# Revit family: TY4651
name_source: partatom
category: Sprinklers
revit_build: Autodesk Revit 2016 (Build: 20150220_1215(x64)
units: mm (PartAtom-declared; Revit-internal decimal feet)

## family parameters
Always vertical = Yes
Cut with Voids When Loaded = No
Maintain Annotation Orientation = No
OmniClass Number = 23.65.70.17.11.24
OmniClass Title = Fire Fighting Sprinkler Heads
Part Type = Normal
Room Calculation Point = No
Round Connector Dimension = Use Diameter
Shared = No
Work Plane-Based = No

## types (40) — shared parameters
COBie = Yes
COBie.Component.Name = Sprinklers:Conventional_SIN
COBie.Type = Yes
COBie.Type.AssetType = Fixed
COBie.Type.Category = Pr_70_55_97_84:Sprinklers
COBie.Type.DurationUnit = year
COBie.Type.Manufacturer = Tyco Fire Protection Products
COBie.Type.Material = Bronze
COBie.Type.NominalHeight = 0' - 0"
COBie.Type.NominalLength = 0' - 0"
COBie.Type.NominalWidth = 0' - 0"
Coverage = Standard
K-Factor = 7.9771
Manufacturer = Tyco Fire Protection Products
Manufacturer URL = www.tyco-fire.com
Model = TY-B
Nominal Diameter 1 = 1"
Orifice = Extra Large
Orifice Size = 1"
Outside Diameter 1 = 1"
Response = Standard
SIN No = TY4651
Takeout 1 = 2"
Technical Data Sheet No = TFP661
zero-valued in all types: COBie.Type.ReplacementCost, Style Id

## per-type parameters (varying)
| type | COBie.Component.Description | COBie.Component.InstallationDate | COBie.Component.WarrantyStartDate | COBie.Type.Colour | COBie.Type.Finish | COBie.Type.ModelNumber | COBie.Type.ModelReference | COBie.Type.Shape | COBie.Type.Size | COBie.Type.WarrantyDescription | COBie.Type.WarrantyDurationLabor | COBie.Type.WarrantyDurationParts | COBie.Type.WarrantyDurationUnit | COBie.Type.WarrantyGuarantorParts | Description | Part No | Temperature Rating |
| TY-B Conventional (Old Style) Brass 135°F/57°C 8K ¾" NPT_57-593-1-135 | TY-B Wet Conventional  57.2°C K115 DN20 NPT Br |  |  | Yellow | Natural Brass | 57-593-1-135 | TY-B Wet Conventional  57.2°C K115 DN20 NPT Br | Cylinder | 3/4"(DN20) |  |  |  |  | http://tycofsbp.com | TY-B Conventional (Old Style) Brass 135°F/57°C 8K ¾" NPT_57-593-1-135 | 57-593-1-135 | 135 °F |
| TY-B Conventional (Old Style) Brass 155°F/68°C 8K ¾" NPT_57-593-1-155 | TY-B Wet Conventional  68.3°C K115 DN20 NPT Br |  |  | Yellow | Natural Brass | 57-593-1-155 | TY-B Wet Conventional  68.3°C K115 DN20 NPT Br | Cylinder | 3/4"(DN20) |  |  |  |  | http://tycofsbp.com | TY-B Conventional (Old Style) Brass 155°F/68°C 8K ¾" NPT_57-593-1-155 | 57-593-1-155 | 155 °F |
| TY-B Conventional (Old Style) Brass 175°F/79°C 8K ¾" NPT_57-593-1-175 | TY-B Wet Conventional  79.4°C K115 DN20 NPT Br |  |  | Yellow | Natural Brass | 57-593-1-175 | TY-B Wet Conventional  79.4°C K115 DN20 NPT Br | Cylinder | 3/4"(DN20) |  |  |  |  | http://tycofsbp.com | TY-B Conventional (Old Style) Brass 175°F/79°C 8K ¾" NPT_57-593-1-175 | 57-593-1-175 | 175 °F |
| TY-B Conventional (Old Style) Brass 200°F/93°C 8K ¾" NPT_57-593-1-200 | TY-B Wet Conventional  93.3°C K115 DN20 NPT Br |  |  | Yellow | Natural Brass | 57-593-1-200 | TY-B Wet Conventional  93.3°C K115 DN20 NPT Br | Cylinder | 3/4"(DN20) |  |  |  |  | http://tycofsbp.com | TY-B Conventional (Old Style) Brass 200°F/93°C 8K ¾" NPT_57-593-1-200 | 57-593-1-200 | 200 °F |
| TY-B Conventional (Old Style) Brass 286°F/141°C 8K ¾" NPT_57-593-1-286 | TY-B Wet Conventional  141.1°C K115 DN20 NPT Br |  |  | Yellow | Natural Brass | 57-593-1-286 | TY-B Wet Conventional  141.1°C K115 DN20 NPT Br | Cylinder | 3/4"(DN20) |  |  |  |  | http://tycofsbp.com | TY-B Conventional (Old Style) Brass 286°F/141°C 8K ¾" NPT_57-593-1-286 | 57-593-1-286 | 286 °F |
| TY-B Conventional (Old Style) Brass 360°F/182°C 8K ¾" NPT_57-593-1-360 | TY-B Wet Conventional  182.2°C K115 DN20 NPT Br | 1900-12-31T23:59:59 | 1900-12-31T23:59:59 |  |  | 57-593-1-360 | TY-B Wet Conventional  182.2°C K115 DN20 NPT Br |  | DN20 | On-site Sprinkler Replacement Warranty | 10 | 10 | year |  | TY-B Conventional (Old Style) Brass 360°F/182°C 8K ¾" NPT_57-593-1-360 | 57-593-1-360 | 360 °F |
| TY-B Conventional (Old Style) White 135°F/57°C 8K ¾" NPT_57-593-3-135 | TY-B Wet Conventional  57.2°C K115 DN20 NPT Wh9010 |  |  | White | Pure White | 57-593-3-135 | TY-B Wet Conventional  57.2°C K115 DN20 NPT Wh9010 | Cylinder | 3/4"(DN20) |  |  |  |  | http://tycofsbp.com | TY-B Conventional (Old Style) Brass 135°F/57°C 8K ¾" NPT_57-593-3-135 | 57-593-3-135 | 135 °F |
| TY-B Conventional (Old Style) White 155°F/68°C 8K ¾" NPT_57-593-3-155 | TY-B Wet Conventional  68.3°C K115 DN20 NPT Wh9010 | 1900-12-31T23:59:59 | 1900-12-31T23:59:59 |  |  | 57-593-3-155 | TY-B Wet Conventional  68.3°C K115 DN20 NPT Wh9010 |  | DN20 | On-site Sprinkler Replacement Warranty | 10 | 10 | year |  | TY-B Conventional (Old Style) Brass 155°F/68°C 8K ¾" NPT_57-593-3-155 | 57-593-3-155 | 155 °F |
| TY-B Conventional (Old Style) White 175°F/79°C 8K ¾" NPT_57-593-3-175 | TY-B Wet Conventional  79.4°C K115 DN20 NPT Wh9010 |  |  | White | Pure White | 57-593-3-175 | TY-B Wet Conventional  79.4°C K115 DN20 NPT Wh9010 | Cylinder | 3/4"(DN20) |  |  |  |  | http://tycofsbp.com | TY-B Conventional (Old Style) Brass 175°F/79°C 8K ¾" NPT_57-593-3-175 | 57-593-3-175 | 175 °F |
| TY-B Conventional (Old Style) White 200°F/93°C 8K ¾" NPT_57-593-3-200 | TY-B Wet Conventional  93.3°C K115 DN20 NPT Wh9010 |  |  | White | Pure White | 57-593-3-200 | TY-B Wet Conventional  93.3°C K115 DN20 NPT Wh9010 | Cylinder | 3/4"(DN20) |  |  |  |  | http://tycofsbp.com | TY-B Conventional (Old Style) Brass 200°F/93°C 8K ¾" NPT_57-593-3-200 | 57-593-3-200 | 200 °F |
| TY-B Conventional (Old Style) White 286°F/141°C 8K ¾" NPT_57-593-3-286 | TY-B Wet Conventional  141.1°C K115 DN20 NPT Wh9010 |  |  | White | Pure White | 57-593-3-286 | TY-B Wet Conventional  141.1°C K115 DN20 NPT Wh9010 | Cylinder | 3/4"(DN20) |  |  |  |  | http://tycofsbp.com | TY-B Conventional (Old Style) Brass 286°F/141°C 8K ¾" NPT_57-593-3-286 | 57-593-3-286 | 286 °F |
| TY-B Conventional (Old Style) White 360°F/182°C 8K ¾" NPT_57-593-3-360 | TY-B Wet Conventional  182.2°C K115 DN20 NPT Wh9010 |  |  | White | Pure White | 57-593-3-360 | TY-B Wet Conventional  182.2°C K115 DN20 NPT Wh9010 | Cylinder | 3/4"(DN20) |  |  |  |  | http://tycofsbp.com | TY-B Conventional (Old Style) Brass 360°F/182°C 8K ¾" NPT_57-593-3-360 | 57-593-3-360 | 360 °F |
| TY-B Conventional (Old Style) White 135°F/57°C 8K ¾" NPT_57-593-4-135 | TY-B Wet Conventional  57.2°C K115 DN20 NPT Wh9003 |  |  | White | Signal White | 57-593-4-135 | TY-B Wet Conventional  57.2°C K115 DN20 NPT Wh9003 | Cylinder | 3/4"(DN20) |  |  |  |  | http://tycofsbp.com | TY-B Conventional (Old Style) White 135°F/57°C 8K ¾" NPT_57-593-4-135 | 57-593-4-135 | 135 °F |
| TY-B Conventional (Old Style) White 155°F/68°C 8K ¾" NPT_57-593-4-155 | TY-B Wet Conventional  68.3°C K115 DN20 NPT Wh9003 |  |  | White | Signal White | 57-593-4-155 | TY-B Wet Conventional  68.3°C K115 DN20 NPT Wh9003 | Cylinder | 3/4"(DN20) |  |  |  |  | http://tycofsbp.com | TY-B Conventional (Old Style) White 155°F/68°C 8K ¾" NPT_57-593-4-155 | 57-593-4-155 | 155 °F |
| TY-B Conventional (Old Style) White 175°F/79°C 8K ¾" NPT_57-593-4-175 | TY-B Wet Conventional  79.4°C K115 DN20 NPT Wh9003 |  |  | White | Signal White | 57-593-4-175 | TY-B Wet Conventional  79.4°C K115 DN20 NPT Wh9003 | Cylinder | 3/4"(DN20) |  |  |  |  | http://tycofsbp.com | TY-B Conventional (Old Style) White 175°F/79°C 8K ¾" NPT_57-593-4-175 | 57-593-4-175 | 175 °F |
| TY-B Conventional (Old Style) White 200°F/93°C 8K ¾" NPT_57-593-4-200 | TY-B Wet Conventional  93.3°C K115 DN20 NPT Wh9003 |  |  | White | Signal White | 57-593-4-200 | TY-B Wet Conventional  93.3°C K115 DN20 NPT Wh9003 | Cylinder | 3/4"(DN20) |  |  |  |  | http://tycofsbp.com | TY-B Conventional (Old Style) White 200°F/93°C 8K ¾" NPT_57-593-4-200 | 57-593-4-200 | 200 °F |
| TY-B Conventional (Old Style) White 286°F/141°C 8K ¾" NPT_57-593-4-286 | TY-B Wet Conventional  141.1°C K115 DN20 NPT Wh9003 |  |  | White | Signal White | 57-593-4-286 | TY-B Wet Conventional  141.1°C K115 DN20 NPT Wh9003 | Cylinder | 3/4"(DN20) |  |  |  |  | http://tycofsbp.com | TY-B Conventional (Old Style) White 286°F/141°C 8K ¾" NPT_57-593-4-286 | 57-593-4-286 | 286 °F |
| TY-B Conventional (Old Style) White 360°F/182°C 8K ¾" NPT_57-593-4-360 | TY-B Wet Conventional  182.2°C K115 DN20 NPT Wh9003 |  |  | White | Signal White | 57-593-4-360 | TY-B Wet Conventional  182.2°C K115 DN20 NPT Wh9003 | Cylinder | 3/4"(DN20) |  |  |  |  | http://tycofsbp.com | TY-B Conventional (Old Style) White 360°F/182°C 8K ¾" NPT_57-593-4-360 | 57-593-4-360 | 360 °F |
| TY-B Conventional (Old Style) Wax 135°F/57°C 8K ¾" NPT_57-593-6-135 | TY-B Wet Conventional  57.2°C K115 DN20 NPT Wx |  |  | Gray | Wax Coated | 57-593-6-135 | TY-B Wet Conventional  57.2°C K115 DN20 NPT Wx | Cylinder | 3/4"(DN20) |  |  |  |  | http://tycofsbp.com | TY-B Conventional (Old Style) Wax 135°F/57°C 8K ¾" NPT_57-593-6-135 | 57-593-6-135 | 135 °F |
| TY-B Conventional (Old Style) Wax 155°F/68°C 8K ¾" NPT_57-593-6-155 | TY-B Wet Conventional  68.3°C K115 DN20 NPT Wx |  |  | Gray | Wax Coated | 57-593-6-155 | TY-B Wet Conventional  68.3°C K115 DN20 NPT Wx | Cylinder | 3/4"(DN20) |  |  |  |  | http://tycofsbp.com | TY-B Conventional (Old Style) Wax 155°F/68°C 8K ¾" NPT_57-593-6-155 | 57-593-6-155 | 155 °F |
| TY-B Conventional (Old Style) Wax 175°F/79°C 8K ¾" NPT_57-593-6-175 | TY-B Wet Conventional  79.4°C K115 DN20 NPT Wx |  |  | Gray | Wax Coated | 57-593-6-175 | TY-B Wet Conventional  79.4°C K115 DN20 NPT Wx | Cylinder | 3/4"(DN20) |  |  |  |  | http://tycofsbp.com | TY-B Conventional (Old Style) Wax 175°F/79°C 8K ¾" NPT_57-593-6-175 | 57-593-6-175 | 175 °F |
| TY-B Conventional (Old Style) Wax 200°F/93°C 8K ¾" NPT_57-593-6-200 | TY-B Wet Conventional  93.3°C K115 DN20 NPT Wx |  |  | Gray | Wax Coated | 57-593-6-200 | TY-B Wet Conventional  93.3°C K115 DN20 NPT Wx | Cylinder | 3/4"(DN20) |  |  |  |  | http://tycofsbp.com | TY-B Conventional (Old Style) Wax 200°F/93°C 8K ¾" NPT_57-593-6-200 | 57-593-6-200 | 200 °F |
| TY-B Conventional (Old Style) Wax 286°F/141°C 8K ¾" NPT_57-593-6-286 | TY-B Wet Conventional  141.1°C K115 DN20 NPT Wx |  |  | Gray | Wax Coated | 57-593-6-286 | TY-B Wet Conventional  141.1°C K115 DN20 NPT Wx | Cylinder | 3/4"(DN20) |  |  |  |  | http://tycofsbp.com | TY-B Conventional (Old Style) Wax 286°F/141°C 8K ¾" NPT_57-593-6-286 | 57-593-6-286 | 286 °F |
| TY-B Conventional (Old Style) Lead 135°F/57°C 8K ¾" NPT_57-593-7-135 | TY-B Wet Conventional  57.2°C K115 DN20 NPT Lead |  |  | Gray | Lead Coated | 57-593-7-135 | TY-B Wet Conventional  57.2°C K115 DN20 NPT Lead | Cylinder | 3/4"(DN20) |  |  |  |  | http://tycofsbp.com | TY-B Conventional (Old Style) Lead 135°F/57°C 8K ¾" NPT_57-593-7-135 | 57-593-7-135 | 135 °F |
| TY-B Conventional (Old Style) Lead 155°F/68°C 8K ¾" NPT_57-593-7-155 | TY-B Wet Conventional  68.3°C K115 DN20 NPT Lead |  |  | Gray | Lead Coated | 57-593-7-155 | TY-B Wet Conventional  68.3°C K115 DN20 NPT Lead | Cylinder | 3/4"(DN20) |  |  |  |  | http://tycofsbp.com | TY-B Conventional (Old Style) Lead 155°F/68°C 8K ¾" NPT_57-593-7-155 | 57-593-7-155 | 155 °F |
| TY-B Conventional (Old Style) Lead 175°F/79°C 8K ¾" NPT_57-593-7-175 | TY-B Wet Conventional  79.4°C K115 DN20 NPT Lead |  |  | Gray | Lead Coated | 57-593-7-175 | TY-B Wet Conventional  79.4°C K115 DN20 NPT Lead | Cylinder | 3/4"(DN20) |  |  |  |  | http://tycofsbp.com | TY-B Conventional (Old Style) Lead 175°F/79°C 8K ¾" NPT_57-593-7-175 | 57-593-7-175 | 175 °F |
| TY-B Conventional (Old Style) Lead 200°F/93°C 8K ¾" NPT_57-593-7-200 | TY-B Wet Conventional  93.3°C K115 DN20 NPT Lead |  |  | Gray | Lead Coated | 57-593-7-200 | TY-B Wet Conventional  93.3°C K115 DN20 NPT Lead | Cylinder | 3/4"(DN20) |  |  |  |  | http://tycofsbp.com | TY-B Conventional (Old Style) Lead 200°F/93°C 8K ¾" NPT_57-593-7-200 | 57-593-7-200 | 200 °F |
| TY-B Conventional (Old Style) Lead 286°F/141°C 8K ¾" NPT_57-593-7-286 | TY-B Wet Conventional  141.1°C K115 DN20 NPT Lead |  |  | Gray | Lead Coated | 57-593-7-286 | TY-B Wet Conventional  141.1°C K115 DN20 NPT Lead | Cylinder | 3/4"(DN20) |  |  |  |  | http://tycofsbp.com | TY-B Conventional (Old Style) Lead 286°F/141°C 8K ¾" NPT_57-593-7-286 | 57-593-7-286 | 286 °F |
| TY-B Conventional (Old Style) Lead 360°F/182°C 8K ¾" NPT_57-593-7-360 | TY-B Wet Conventional  182.2°C K115 DN20 NPT Lead |  |  | Gray | Lead Coated | 57-593-7-360 | TY-B Wet Conventional  182.2°C K115 DN20 NPT Lead | Cylinder | 3/4"(DN20) |  |  |  |  | http://tycofsbp.com | TY-B Conventional (Old Style) Lead 360°F/182°C 8K ¾" NPT_57-593-7-360 | 57-593-7-360 | 360 °F |
| TY-B Conventional (Old Style) Wax Over Lead 135°F/57°C 8K ¾" NPT_57-593-8-135 | TY-B Wet Conventional  57.2°C K115 DN20 NPT WoL |  |  | Gray | Wax Over Lead | 57-593-8-135 | TY-B Wet Conventional  57.2°C K115 DN20 NPT WoL | Cylinder | 3/4"(DN20) |  |  |  |  | http://tycofsbp.com | TY-B Conventional (Old Style) Wax Over Lead 135°F/57°C 8K ¾" NPT_57-593-8-135 | 57-593-8-135 | 135 °F |
| TY-B Conventional (Old Style) Wax Over Lead 155°F/68°C 8K ¾" NPT_57-593-8-155 | TY-B Wet Conventional  68.3°C K115 DN20 NPT WoL |  |  | Gray | Wax Over Lead | 57-593-8-155 | TY-B Wet Conventional  68.3°C K115 DN20 NPT WoL | Cylinder | 3/4"(DN20) |  |  |  |  | http://tycofsbp.com | TY-B Conventional (Old Style) Wax Over Lead 155°F/68°C 8K ¾" NPT_57-593-8-155 | 57-593-8-155 | 155 °F |
| TY-B Conventional (Old Style) Wax Over Lead 175°F/79°C 8K ¾" NPT_57-593-8-175 | TY-B Wet Conventional  79.4°C K115 DN20 NPT WoL |  |  | Gray | Wax Over Lead | 57-593-8-175 | TY-B Wet Conventional  79.4°C K115 DN20 NPT WoL | Cylinder | 3/4"(DN20) |  |  |  |  | http://tycofsbp.com | TY-B Conventional (Old Style) Wax Over Lead 175°F/79°C 8K ¾" NPT_57-593-8-175 | 57-593-8-175 | 175 °F |
| TY-B Conventional (Old Style) Wax Over Lead 200°F/93°C 8K ¾" NPT_57-593-8-200 | TY-B Wet Conventional  93.3°C K115 DN20 NPT WoL |  |  | Gray | Wax Over Lead | 57-593-8-200 | TY-B Wet Conventional  93.3°C K115 DN20 NPT WoL | Cylinder | 3/4"(DN20) |  |  |  |  | http://tycofsbp.com | TY-B Conventional (Old Style) Wax Over Lead 200°F/93°C 8K ¾" NPT_57-593-8-200 | 57-593-8-200 | 200 °F |
| TY-B Conventional (Old Style) Wax Over Lead 286°F/141°C 8K ¾" NPT_57-593-8-286 | TY-B Wet Conventional  141.1°C K115 DN20 NPT WoL |  |  | Gray | Wax Over Lead | 57-593-8-286 | TY-B Wet Conventional  141.1°C K115 DN20 NPT WoL | Cylinder | 3/4"(DN20) |  |  |  |  | http://tycofsbp.com | TY-B Conventional (Old Style) Wax Over Lead 286°F/141°C 8K ¾" NPT_57-593-8-286 | 57-593-8-286 | 286 °F |
| TY-B Conventional (Old Style) Chrome 135°F/57°C 8K ¾" NPT_57-593-9-135 | TY-B Wet Conventional  57.2°C K115 DN20 NPT Chr |  |  | Silver | Chrome Plated | 57-593-9-135 | TY-B Wet Conventional  57.2°C K115 DN20 NPT Chr | Cylinder | 3/4"(DN20) |  |  |  |  | http://tycofsbp.com | TY-B Conventional (Old Style) Chrome 135°F/57°C 8K ¾" NPT_57-593-9-135 | 57-593-9-135 | 135 °F |
| TY-B Conventional (Old Style) Chrome 155°F/68°C 8K ¾" NPT_57-593-9-155 | TY-B Wet Conventional  68.3°C K115 DN20 NPT Chr |  |  | Silver | Chrome Plated | 57-593-9-155 | TY-B Wet Conventional  68.3°C K115 DN20 NPT Chr | Cylinder | 3/4"(DN20) |  |  |  |  | http://tycofsbp.com | TY-B Conventional (Old Style) Chrome 155°F/68°C 8K ¾" NPT_57-593-9-155 | 57-593-9-155 | 155 °F |
| TY-B Conventional (Old Style) Chrome 175°F/79°C 8K ¾" NPT_57-593-9-175 | TY-B Wet Conventional  79.4°C K115 DN20 NPT Chr |  |  | Silver | Chrome plated | 57-593-9-175 | TY-B Wet Conventional  79.4°C K115 DN20 NPT Chr | Cylinder | 3/4"(DN20) |  |  |  |  | http://tycofsbp.com | TY-B Conventional (Old Style) Chrome 175°F/79°C 8K ¾" NPT_57-593-9-175 | 57-593-9-175 | 175 °F |
| TY-B Conventional (Old Style) Chrome 200°F/93°C 8K ¾" NPT_57-593-9-200 | TY-B Wet Conventional  93.3°C K115 DN20 NPT Chr |  |  | Silver | Chrome Plated | 57-593-9-200 | TY-B Wet Conventional  93.3°C K115 DN20 NPT Chr | Cylinder | 3/4"(DN20) |  |  |  |  | http://tycofsbp.com | TY-B Conventional (Old Style) Chrome 200°F/93°C 8K ¾" NPT_57-593-9-200 | 57-593-9-200 | 200 °F |
| TY-B Conventional (Old Style) Chrome 286°F/141°C 8K ¾" NPT_57-593-9-286 | TY-B Wet Conventional  141.1°C K115 DN20 NPT Chr |  |  | Silver | Chrome Plated | 57-593-9-286 | TY-B Wet Conventional  141.1°C K115 DN20 NPT Chr | Cylinder | 3/4"(DN20) |  |  |  |  | http://tycofsbp.com | TY-B Conventional (Old Style) Chrome 286°F/141°C 8K ¾" NPT_57-593-9-286 | 57-593-9-286 | 286 °F |
| TY-B Conventional (Old Style) Chrome 360°F/182°C 8K ¾" NPT_57-593-9-360 | TY-B Wet Conventional  182.2°C K115 DN20 NPT Chr |  |  | Silver | Chrome plated | 57-593-9-360 | TY-B Wet Conventional  182.2°C K115 DN20 NPT Chr | Cylinder | 3/4"(DN20) |  |  |  |  | http://tycofsbp.com | TY-B Conventional (Old Style) Chrome 360°F/182°C 8K ¾" NPT_57-593-9-360 | 57-593-9-360 | 360 °F |

## geometry (parser evidence)
native form markers: Blend x4, Sweep x47
no freeform markers — native parametric forms only
